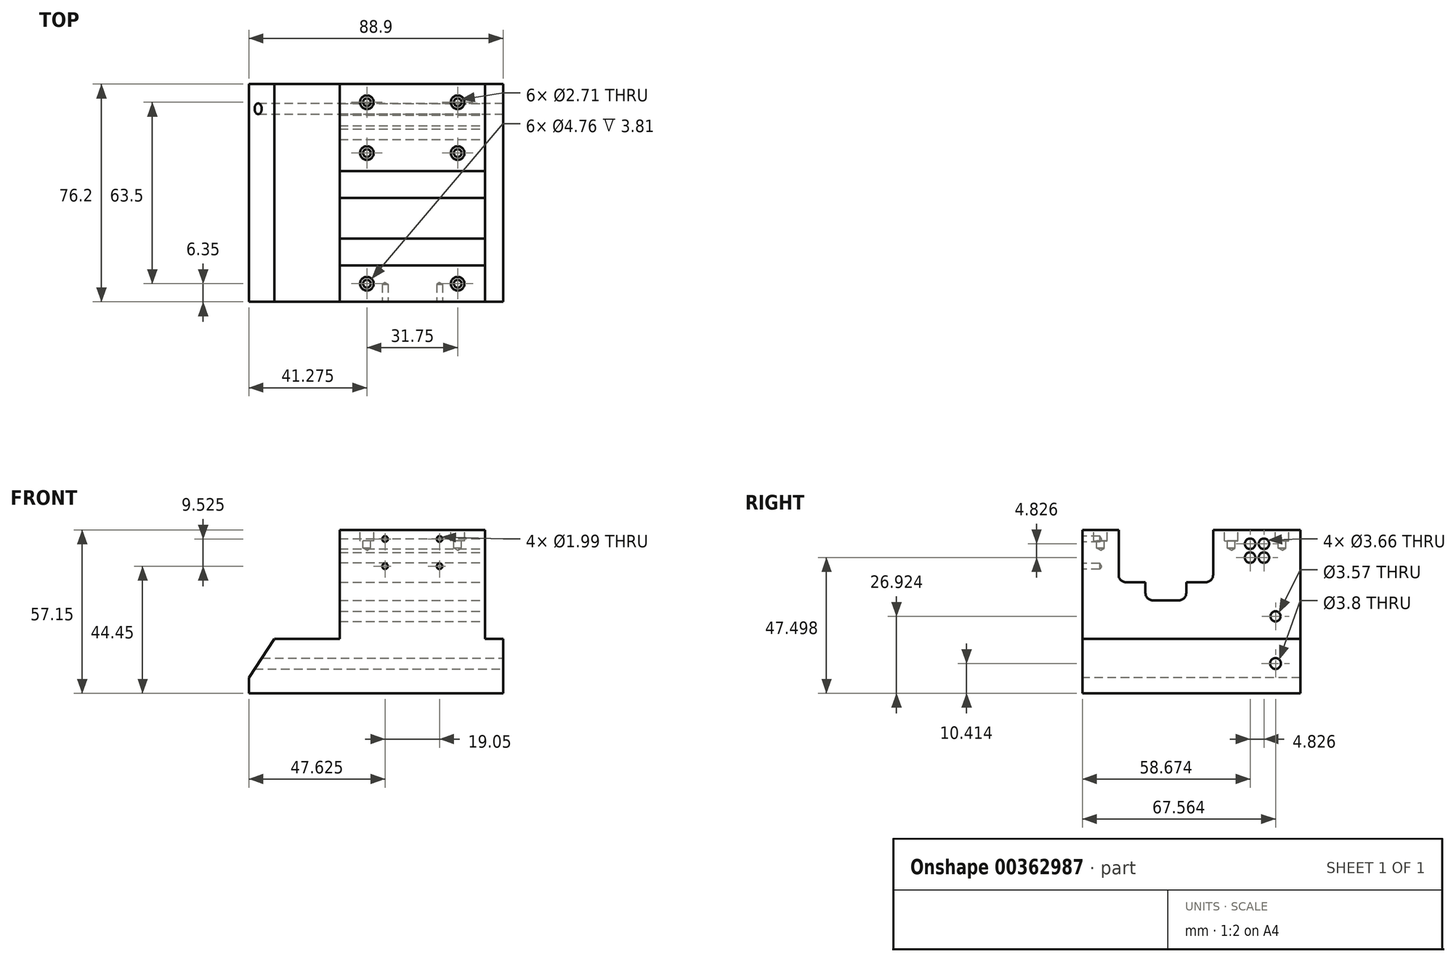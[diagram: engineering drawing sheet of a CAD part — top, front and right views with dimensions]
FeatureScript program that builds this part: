
annotation { "Feature Type Name" : "Feature", "Feature Type Description" : "" }
export const myFeature = defineFeature(function(context is Context, id is Id, definition is map)
    precondition{}
    {
        {
            var Q0;
            Q0=qCreatedBy(makeId("Front.planeOp"),FACE);
            var sketch = newSketch(context, id + "F0", { "sketchPlane" : qUnion([Q0])});
            skLineSegment(sketch, "E0", {"start": v(0, 0) * mm, "end": v(88.9, 0) * mm});
            skLineSegment(sketch, "E1", {"start": v(88.9, 0) * mm, "end": v(88.9, 19.05) * mm});
            skLineSegment(sketch, "E2", {"start": v(88.9, 19.05) * mm, "end": v(8.97, 19.05) * mm});
            skLineSegment(sketch, "E3", {"start": v(0, 5.49) * mm, "end": v(0, 0) * mm});
            skLineSegment(sketch, "E4", {"start": v(0, 5.49) * mm, "end": v(8.97, 19.05) * mm});
            skPoint(sketch, "E5.orphan", {"position": v(0, 19.05) * mm});
            skLineSegment(sketch, "E6", {"start": v(82.55, 19.05) * mm, "end": v(82.55, 57.15) * mm});
            skLineSegment(sketch, "E7", {"start": v(82.55, 57.15) * mm, "end": v(31.75, 57.15) * mm});
            skLineSegment(sketch, "E8", {"start": v(31.75, 57.15) * mm, "end": v(31.75, 19.05) * mm});
            skSolve(sketch);
        }
        {
            var Q0;
            Q0=makeQuery(id+"F0.imprint","IMPRINT",FACE,{"disambiguationData":[TD([[makeQuery(id+"F0.imprint","IMPRINT",EDGE,{"derivedFrom":sQuery(id+"F0.wireOp",EDGE,"E0")}),1.0]])]});
            var Q1;
            {var subQ0=sQuery(id+"F0.wireOp",EDGE,"E6");Q1=makeQuery(id+"F0.imprint","IMPRINT",FACE,{"disambiguationData":[TD([[makeQuery(id+"F0.imprint","IMPRINT",EDGE,{"derivedFrom":subQ0}),1.0]])]});}
            extrude(context, id + "F1", {"entities" : qUnion([Q0, Q1]), "oppositeDirection" : true, "depth" : 76.2 * mm});
        }
        {
            var Q0;
            Q0=makeQuery(id+"F1.opExtrude","SWEPT_FACE",FACE,{"disambiguationData":[OSD([sQuery(id+"F0.wireOp",EDGE,"E6")])]});
            var sketch = newSketch(context, id + "F2", { "sketchPlane" : qUnion([Q0])});
            skLineSegment(sketch, "E9.0", {"start": v(0, 19.05) * mm, "end": v(0, 57.15) * mm});
            skLineSegment(sketch, "E10.0", {"start": v(76.2, 57.15) * mm, "end": v(0, 57.15) * mm});
            skLineSegment(sketch, "E11.0", {"start": v(43.18, 38.86) * mm, "end": v(36.32, 38.86) * mm});
            skLineSegment(sketch, "E12.0", {"start": v(36.32, 35.05) * mm, "end": v(36.32, 38.86) * mm});
            skLineSegment(sketch, "E13.0", {"start": v(22.1, 35.05) * mm, "end": v(22.1, 38.86) * mm});
            skLineSegment(sketch, "E14.trimOffspring", {"start": v(12.7, 41.4) * mm, "end": v(12.7, 57.15) * mm});
            skLineSegment(sketch, "E15.trimOffspring", {"start": v(22.1, 38.86) * mm, "end": v(15.24, 38.86) * mm});
            skLineSegment(sketch, "E16.trimOffspring", {"start": v(45.72, 41.4) * mm, "end": v(45.72, 57.15) * mm});
            skLineSegment(sketch, "E17.trimOffspring", {"start": v(33.78, 32.51) * mm, "end": v(24.64, 32.51) * mm});
            skPoint(sketch, "E18.visualSharp", {"position": v(12.7, 38.86) * mm});
            skArc(sketch, "E18.filletArc", {"start": v(12.7, 41.4) * mm, "mid": v(13.44, 39.6) * mm, "end": v(15.24, 38.86) * mm});
            skPoint(sketch, "E19.visualSharp", {"position": v(22.1, 32.51) * mm});
            skArc(sketch, "E19.filletArc", {"start": v(22.1, 35.05) * mm, "mid": v(22.84, 33.26) * mm, "end": v(24.64, 32.51) * mm});
            skPoint(sketch, "E20.visualSharp", {"position": v(36.32, 32.51) * mm});
            skArc(sketch, "E20.filletArc", {"start": v(33.78, 32.51) * mm, "mid": v(35.58, 33.26) * mm, "end": v(36.32, 35.05) * mm});
            skPoint(sketch, "E21.visualSharp", {"position": v(45.72, 38.86) * mm});
            skArc(sketch, "E21.filletArc", {"start": v(43.18, 38.86) * mm, "mid": v(44.98, 39.6) * mm, "end": v(45.72, 41.4) * mm});
            skPoint(sketch, "E22", {"position": v(58.67, 52.32) * mm});
            skPoint(sketch, "E23", {"position": v(63.5, 52.32) * mm});
            skPoint(sketch, "E24", {"position": v(63.5, 47.5) * mm});
            skPoint(sketch, "E25", {"position": v(58.67, 47.5) * mm});
            skPoint(sketch, "E26", {"position": v(67.56, 10.41) * mm});
            skPoint(sketch, "E27", {"position": v(67.56, 26.92) * mm});
            skSolve(sketch);
        }
        {
            var Q0;
            Q0=makeQuery(id+"F2.imprint","IMPRINT",FACE,{"disambiguationData":[TD([[makeQuery(id+"F2.imprint","IMPRINT",EDGE,{"derivedFrom":sQuery(id+"F2.wireOp",EDGE,"E11.0")}),-1.0]])]});
            extrude(context, id + "F3", {"entities" : qUnion([Q0]), "operationType" : NewBodyOperationType.REMOVE, "endBound" : BoundingType.THROUGH_ALL, "oppositeDirection" : true, "depth" : 25.4 * mm});
        }
        {
            var Q0;
            Q0=sQuery(id+"F2.wireOp",VERTEX,"E22");
            var Q1;
            Q1=sQuery(id+"F2.wireOp",VERTEX,"E23");
            var Q2;
            Q2=sQuery(id+"F2.wireOp",VERTEX,"E24");
            var Q3;
            Q3=sQuery(id+"F2.wireOp",VERTEX,"E25");
            var Q4;
            Q4=makeQuery(id+"F1.opExtrude","SWEPT_BODY",BODY,{"disambiguationData":[OSD([sQuery(id+"F0.wireOp",EDGE,"E0"),sQuery(id+"F0.wireOp",EDGE,"E1"),sQuery(id+"F0.wireOp",EDGE,"E2"),sQuery(id+"F0.wireOp",EDGE,"E3"),sQuery(id+"F0.wireOp",EDGE,"E4"),sQuery(id+"F0.wireOp",EDGE,"E6"),sQuery(id+"F0.wireOp",EDGE,"E7"),sQuery(id+"F0.wireOp",EDGE,"E8")])]});
            hole(context, id + "F4", {"style" : HoleStyle.SIMPLE, "endStyle" : HoleEndStyle.THROUGH, "standardTappedOrClearance" : lookupTablePath({ "standard" : "ANSI", "size" : "#27 (0.14)", "type" : "Drilled" }), "standardBlindInLast" : lookupTablePath({ "standard" : "ANSI", "size" : "#27", "type" : "Drilled" }), "holeDiameter" : 3.66 * mm, "tappedDepth" : 5.4 * mm, "tapClearance" : 3, "locations" : qUnion([Q0, Q1, Q2, Q3]), "scope" : qUnion([Q4])});
        }
        {
            var Q0;
            Q0=sQuery(id+"F2.wireOp",VERTEX,"E27");
            var Q1;
            Q1=makeQuery(id+"F1.opExtrude","SWEPT_BODY",BODY,{"disambiguationData":[OSD([sQuery(id+"F0.wireOp",EDGE,"E0"),sQuery(id+"F0.wireOp",EDGE,"E1"),sQuery(id+"F0.wireOp",EDGE,"E2"),sQuery(id+"F0.wireOp",EDGE,"E3"),sQuery(id+"F0.wireOp",EDGE,"E4"),sQuery(id+"F0.wireOp",EDGE,"E6"),sQuery(id+"F0.wireOp",EDGE,"E7"),sQuery(id+"F0.wireOp",EDGE,"E8")])]});
            hole(context, id + "F5", {"style" : HoleStyle.SIMPLE, "endStyle" : HoleEndStyle.THROUGH, "standardTappedOrClearance" : lookupTablePath({ "standard" : "ANSI", "size" : "#28 (0.14)", "type" : "Drilled" }), "standardBlindInLast" : lookupTablePath({ "standard" : "ANSI", "size" : "#28", "type" : "Drilled" }), "holeDiameter" : 3.57 * mm, "tappedDepth" : 5.4 * mm, "tapClearance" : 3, "locations" : qUnion([Q0]), "scope" : qUnion([Q1])});
        }
        {
            var Q0;
            Q0=makeQuery(id+"F1.opExtrude","SWEPT_FACE",FACE,{"disambiguationData":[OSD([sQuery(id+"F0.wireOp",EDGE,"E1")])]});
            var sketch = newSketch(context, id + "F6", { "sketchPlane" : qUnion([Q0])});
            skPoint(sketch, "E28.0", {"position": v(67.56, 10.41) * mm});
            skSolve(sketch);
        }
        {
            var Q0;
            Q0=sQuery(id+"F6.wireOp",VERTEX,"E28.0");
            var Q1;
            Q1=makeQuery(id+"F1.opExtrude","SWEPT_BODY",BODY,{"disambiguationData":[OSD([sQuery(id+"F0.wireOp",EDGE,"E0"),sQuery(id+"F0.wireOp",EDGE,"E1"),sQuery(id+"F0.wireOp",EDGE,"E2"),sQuery(id+"F0.wireOp",EDGE,"E3"),sQuery(id+"F0.wireOp",EDGE,"E4"),sQuery(id+"F0.wireOp",EDGE,"E6"),sQuery(id+"F0.wireOp",EDGE,"E7"),sQuery(id+"F0.wireOp",EDGE,"E8")])]});
            hole(context, id + "F7", {"style" : HoleStyle.SIMPLE, "endStyle" : HoleEndStyle.THROUGH, "standardTappedOrClearance" : lookupTablePath({ "standard" : "ANSI", "size" : "#25 (0.15)", "type" : "Drilled" }), "standardBlindInLast" : lookupTablePath({ "standard" : "ANSI", "size" : "#25", "type" : "Drilled" }), "holeDiameter" : 3.8 * mm, "tappedDepth" : 5.4 * mm, "tapClearance" : 3, "locations" : qUnion([Q0]), "scope" : qUnion([Q1])});
        }
        {
            var Q0;
            Q0=makeQuery(id+"F1.opExtrude","CAP_FACE",FACE,{"disambiguationData":[OSD([sQuery(id+"F0.wireOp",EDGE,"E0"),sQuery(id+"F0.wireOp",EDGE,"E1"),sQuery(id+"F0.wireOp",EDGE,"E2"),sQuery(id+"F0.wireOp",EDGE,"E3"),sQuery(id+"F0.wireOp",EDGE,"E4"),sQuery(id+"F0.wireOp",EDGE,"E6"),sQuery(id+"F0.wireOp",EDGE,"E7"),sQuery(id+"F0.wireOp",EDGE,"E8")])],"isStart":true});
            var sketch = newSketch(context, id + "F8", { "sketchPlane" : qUnion([Q0])});
            skPoint(sketch, "E29", {"position": v(47.62, 53.98) * mm});
            skPoint(sketch, "E30", {"position": v(66.67, 53.98) * mm});
            skPoint(sketch, "E31", {"position": v(66.67, 44.45) * mm});
            skPoint(sketch, "E32", {"position": v(47.62, 44.45) * mm});
            skSolve(sketch);
        }
        {
            var Q0;
            Q0=sQuery(id+"F8.wireOp",VERTEX,"E29");
            var Q1;
            Q1=sQuery(id+"F8.wireOp",VERTEX,"E30");
            var Q2;
            Q2=sQuery(id+"F8.wireOp",VERTEX,"E31");
            var Q3;
            Q3=sQuery(id+"F8.wireOp",VERTEX,"E32");
            var Q4;
            Q4=makeQuery(id+"F1.opExtrude","SWEPT_BODY",BODY,{"disambiguationData":[OSD([sQuery(id+"F0.wireOp",EDGE,"E0"),sQuery(id+"F0.wireOp",EDGE,"E1"),sQuery(id+"F0.wireOp",EDGE,"E2"),sQuery(id+"F0.wireOp",EDGE,"E3"),sQuery(id+"F0.wireOp",EDGE,"E4"),sQuery(id+"F0.wireOp",EDGE,"E6"),sQuery(id+"F0.wireOp",EDGE,"E7"),sQuery(id+"F0.wireOp",EDGE,"E8")])]});
            hole(context, id + "F9", {"style" : HoleStyle.SIMPLE, "endStyle" : HoleEndStyle.BLIND, "standardTappedOrClearance" : lookupTablePath({ "standard" : "ANSI", "engagement" : "75%", "pitch" : "48 tpi", "size" : "#3", "type" : "Tapped" }), "standardBlindInLast" : lookupTablePath({ "standard" : "ANSI", "engagement" : "75%", "pitch" : "48 tpi", "size" : "#3", "type" : "Tapped" }), "holeDiameter" : 2 * mm, "showTappedDepth" : true, "holeDepth" : 6.16 * mm, "tappedDepth" : 4.57 * mm, "tapClearance" : 3, "locations" : qUnion([Q0, Q1, Q2, Q3]), "scope" : qUnion([Q4]), "majorDiameter" : 2.5 * mm});
        }
        {
            var Q0;
            {var subQ1=sQuery(id+"F0.wireOp",EDGE,"E7");Q0=makeQuery(id+"F3.boolean.opBoolean","SPLIT",FACE,{"disambiguationData":[TD([makeQuery(id+"F3.opExtrude","SWEPT_FACE",FACE,{"disambiguationData":[OSD([sQuery(id+"F2.wireOp",EDGE,"E16.trimOffspring")])]})])],"derivedFrom":makeQuery(id+"F1.opExtrude","SWEPT_FACE",FACE,{"disambiguationData":[OSD([subQ1])]})});}
            var sketch = newSketch(context, id + "F10", { "sketchPlane" : qUnion([Q0])});
            skPoint(sketch, "E33", {"position": v(41.28, 69.85) * mm});
            skPoint(sketch, "E34", {"position": v(73.03, 69.85) * mm});
            skPoint(sketch, "E35", {"position": v(73.03, 52.07) * mm});
            skPoint(sketch, "E36", {"position": v(41.28, 52.07) * mm});
            skPoint(sketch, "E37", {"position": v(41.28, 6.35) * mm});
            skPoint(sketch, "E38", {"position": v(73.03, 6.35) * mm});
            skSolve(sketch);
        }
        {
            var Q0;
            Q0=sQuery(id+"F10.wireOp",VERTEX,"E33");
            var Q1;
            Q1=sQuery(id+"F10.wireOp",VERTEX,"E36");
            var Q2;
            Q2=sQuery(id+"F10.wireOp",VERTEX,"E34");
            var Q3;
            Q3=sQuery(id+"F10.wireOp",VERTEX,"E35");
            var Q4;
            Q4=sQuery(id+"F10.wireOp",VERTEX,"E38");
            var Q5;
            Q5=sQuery(id+"F10.wireOp",VERTEX,"E37");
            var Q6;
            Q6=makeQuery(id+"F1.opExtrude","SWEPT_BODY",BODY,{"disambiguationData":[OSD([sQuery(id+"F0.wireOp",EDGE,"E0"),sQuery(id+"F0.wireOp",EDGE,"E1"),sQuery(id+"F0.wireOp",EDGE,"E2"),sQuery(id+"F0.wireOp",EDGE,"E3"),sQuery(id+"F0.wireOp",EDGE,"E4"),sQuery(id+"F0.wireOp",EDGE,"E6"),sQuery(id+"F0.wireOp",EDGE,"E7"),sQuery(id+"F0.wireOp",EDGE,"E8")])]});
            hole(context, id + "F11", {"style" : HoleStyle.C_BORE, "endStyle" : HoleEndStyle.BLIND, "holeDiameter" : 2.7 * mm, "cBoreDiameter" : 4.76 * mm, "cBoreDepth" : 3.8 * mm, "holeDepth" : 6.35 * mm, "tappedDepth" : 4.58 * mm, "tapClearance" : 3, "locations" : qUnion([Q0, Q1, Q2, Q3, Q4, Q5]), "scope" : qUnion([Q6])});
        }
    });
